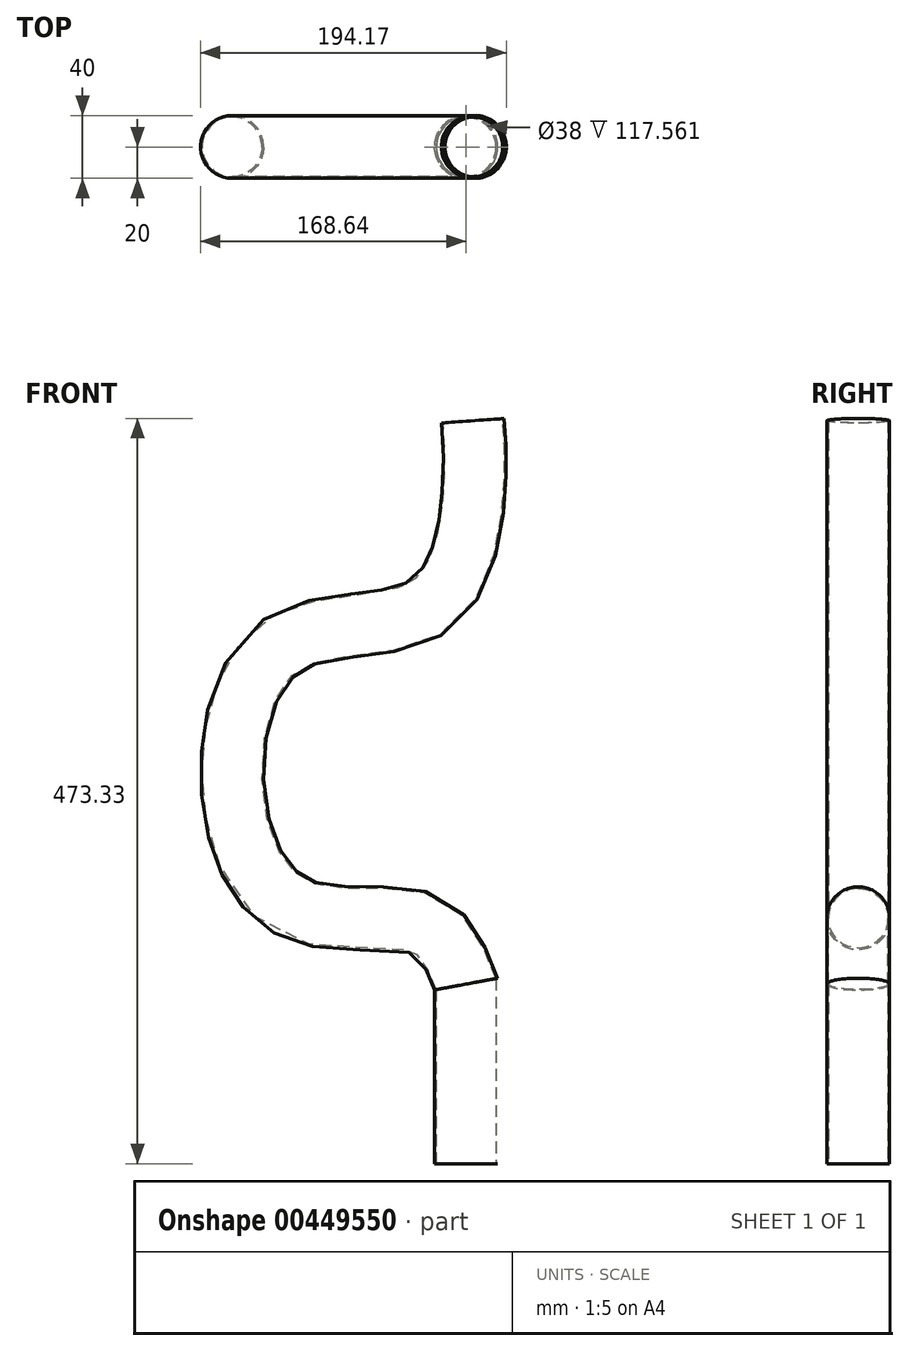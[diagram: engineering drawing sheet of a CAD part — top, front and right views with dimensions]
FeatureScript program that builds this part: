
annotation { "Feature Type Name" : "Feature", "Feature Type Description" : "" }
export const myFeature = defineFeature(function(context is Context, id is Id, definition is map)
    precondition{}
    {
        {
            var Q0;
            Q0=qCreatedBy(makeId("Top.planeOp"),FACE);
            var sketch = newSketch(context, id + "F0", { "sketchPlane" : qUnion([Q0])});
            skCircle(sketch, "E0", {"center": v(0, 0) * mm, "radius": 19 * mm});
            skCircle(sketch, "E1", {"center": v(0, 0) * mm, "radius": 20 * mm});
            skSolve(sketch);
        }
        {
            var Q0;
            Q0=qSketchRegion(id+"F0",true);
            extrude(context, id + "F1", {"entities" : qUnion([Q0]), "depth" : 10 * mm});
        }
        {
            var Q0;
            Q0=qCreatedBy(makeId("Front.planeOp"),FACE);
            var sketch = newSketch(context, id + "F2", { "sketchPlane" : qUnion([Q0])});
            skLineSegment(sketch, "E2", {"start": v(0, 0) * mm, "end": v(0, 114.07) * mm});
            skFitSpline(sketch, "E3", {"points": [v(0, 114.07) * mm, v(-26.97, 152.13) * mm, v(-103.64, 160.08) * mm, v(-147.38, 228.8) * mm, v(-116.14, 329.9) * mm, v(-24.13, 353.75) * mm, v(4.84, 425.88) * mm, v(4.27, 471.88) * mm], "startDerivative": vector(-160.71, 422.95) * mm, "endDerivative": vector(-26.16, 361.38) * mm});
            skSolve(sketch);
        }
        {
            var Q0;
            Q0=makeQuery(id+"F1.opExtrude","CAP_FACE",FACE,{"disambiguationData":[OSD([sQuery(id+"F0.wireOp",EDGE,"E0"),sQuery(id+"F0.wireOp",EDGE,"E1")])],"isStart":false});
            var Q1;
            Q1=makeQuery(id+"F1.opExtrude","CAP_EDGE",EDGE,{"disambiguationData":[OSD([sQuery(id+"F0.wireOp",EDGE,"E0")])],"isStart":false});
            var Q2;
            Q2=sQuery(id+"F2.wireOp",EDGE,"E2");
            var Q3;
            Q3=sQuery(id+"F2.wireOp",EDGE,"E3");
            sweep(context, id + "F3", {"operationType" : NewBodyOperationType.ADD, "profiles" : qUnion([Q0]), "surfaceProfiles" : qUnion([Q1]), "path" : qUnion([Q2, Q3])});
        }
    });
